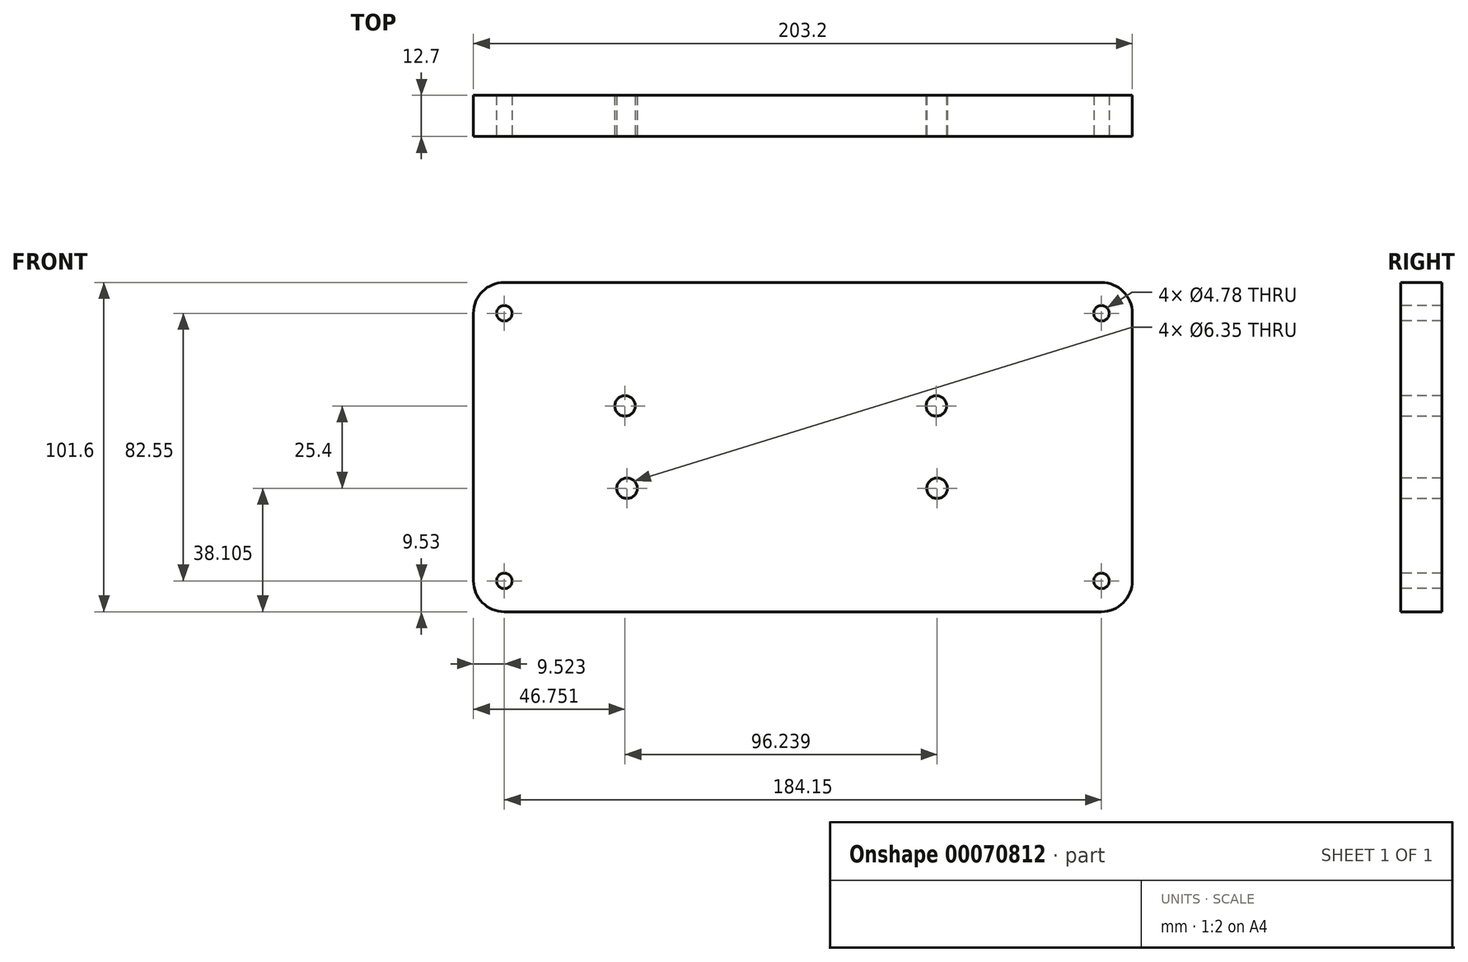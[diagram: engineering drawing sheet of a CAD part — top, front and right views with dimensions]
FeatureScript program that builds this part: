
annotation { "Feature Type Name" : "Feature", "Feature Type Description" : "" }
export const myFeature = defineFeature(function(context is Context, id is Id, definition is map)
    precondition{}
    {
        {
            var Q0;
            Q0=qCreatedBy(makeId("Front.planeOp"),FACE);
            var sketch = newSketch(context, id + "F0", { "sketchPlane" : qUnion([Q0])});
            skLineSegment(sketch, "E0", {"start": v(-110.7, 23.58) * mm, "end": v(-110.7, -78.02) * mm});
            skLineSegment(sketch, "E1", {"start": v(-110.7, -78.02) * mm, "end": v(92.5, -78.02) * mm});
            skLineSegment(sketch, "E2", {"start": v(92.5, -78.02) * mm, "end": v(92.5, 23.58) * mm});
            skLineSegment(sketch, "E3", {"start": v(92.5, 23.58) * mm, "end": v(-110.7, 23.58) * mm});
            skSolve(sketch);
        }
        {
            var Q0;
            Q0 = qSketchRegion(id + "F0", true);
            extrude(context, id + "F1", {"entities" : qUnion([Q0]), "depth" : 12.7 * mm});
        }
        {
            var Q0;
            Q0=makeQuery(id+"F1.opExtrude","SWEPT_EDGE",EDGE,{"disambiguationData":[OSD([sQuery(id+"F0.wireOp",EDGE,"E0"),sQuery(id+"F0.wireOp",EDGE,"E3")])]});
            var Q1;
            Q1=makeQuery(id+"F1.opExtrude","SWEPT_EDGE",EDGE,{"disambiguationData":[OSD([sQuery(id+"F0.wireOp",EDGE,"E0"),sQuery(id+"F0.wireOp",EDGE,"E1")])]});
            var Q2;
            Q2=makeQuery(id+"F1.opExtrude","SWEPT_EDGE",EDGE,{"disambiguationData":[OSD([sQuery(id+"F0.wireOp",EDGE,"E2"),sQuery(id+"F0.wireOp",EDGE,"E3")])]});
            var Q3;
            Q3=makeQuery(id+"F1.opExtrude","SWEPT_EDGE",EDGE,{"disambiguationData":[OSD([sQuery(id+"F0.wireOp",EDGE,"E1"),sQuery(id+"F0.wireOp",EDGE,"E2")])]});
            fillet(context, id + "F2", {"entities" : qUnion([Q0, Q1, Q2, Q3]), "radius" : 9.52 * mm, "tangentPropagation" : true, "allowEdgeOverflow" : false});
        }
        {
            var Q0;
            Q0=makeQuery(id+"F1.opExtrude","CAP_FACE",FACE,{"disambiguationData":[OSD([sQuery(id+"F0.wireOp",EDGE,"E0"),sQuery(id+"F0.wireOp",EDGE,"E1"),sQuery(id+"F0.wireOp",EDGE,"E2"),sQuery(id+"F0.wireOp",EDGE,"E3")])],"isStart":false});
            var sketch = newSketch(context, id + "F3", { "sketchPlane" : qUnion([Q0])});
            skPoint(sketch, "E4", {"position": v(-101.17, 14.06) * mm});
            skPoint(sketch, "E5", {"position": v(82.98, 14.06) * mm});
            skPoint(sketch, "E6", {"position": v(82.98, -68.5) * mm});
            skPoint(sketch, "E7", {"position": v(-101.17, -68.5) * mm});
            skPoint(sketch, "E8", {"position": v(-63.94, -14.52) * mm});
            skPoint(sketch, "E9", {"position": v(-63.32, -39.92) * mm});
            skPoint(sketch, "E10", {"position": v(32.3, -39.92) * mm});
            skPoint(sketch, "E11", {"position": v(32.07, -14.52) * mm});
            skSolve(sketch);
        }
        {
            var Q0;
            Q0=sQuery(id+"F3.wireOp",VERTEX,"E4");
            var Q1;
            Q1=sQuery(id+"F3.wireOp",VERTEX,"E7");
            var Q2;
            Q2=sQuery(id+"F3.wireOp",VERTEX,"E5");
            var Q3;
            Q3=sQuery(id+"F3.wireOp",VERTEX,"E6");
            var Q4;
            Q4=makeQuery(id+"F1.opExtrude","SWEPT_BODY",BODY,{"disambiguationData":[OSD([sQuery(id+"F0.wireOp",EDGE,"E0"),sQuery(id+"F0.wireOp",EDGE,"E1"),sQuery(id+"F0.wireOp",EDGE,"E2"),sQuery(id+"F0.wireOp",EDGE,"E3")])]});
            hole(context, id + "F4", {"style" : HoleStyle.SIMPLE, "holeDiameter" : 4.78 * mm, "endStyle" : HoleEndStyle.THROUGH, "locations" : qUnion([Q0, Q1, Q2, Q3]), "scope" : qUnion([Q4])});
        }
        {
            var Q0;
            Q0=sQuery(id+"F3.wireOp",VERTEX,"E8");
            var Q1;
            Q1=sQuery(id+"F3.wireOp",VERTEX,"E9");
            var Q2;
            Q2=sQuery(id+"F3.wireOp",VERTEX,"E11");
            var Q3;
            Q3=sQuery(id+"F3.wireOp",VERTEX,"E10");
            var Q4;
            Q4=makeQuery(id+"F1.opExtrude","SWEPT_BODY",BODY,{"disambiguationData":[OSD([sQuery(id+"F0.wireOp",EDGE,"E0"),sQuery(id+"F0.wireOp",EDGE,"E1"),sQuery(id+"F0.wireOp",EDGE,"E2"),sQuery(id+"F0.wireOp",EDGE,"E3")])]});
            hole(context, id + "F5", {"style" : HoleStyle.SIMPLE, "holeDiameter" : 6.35 * mm, "endStyle" : HoleEndStyle.THROUGH, "locations" : qUnion([Q0, Q1, Q2, Q3]), "scope" : qUnion([Q4])});
        }
    });
